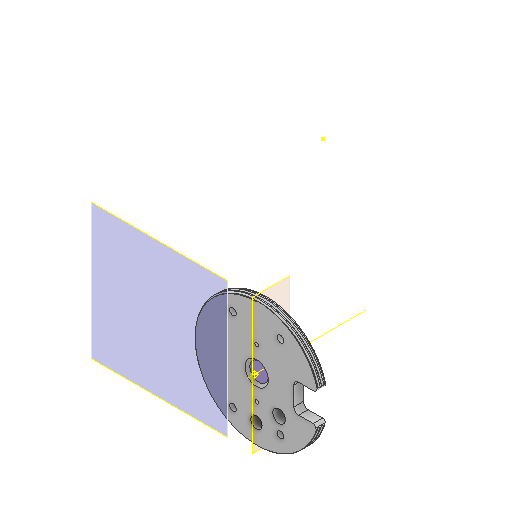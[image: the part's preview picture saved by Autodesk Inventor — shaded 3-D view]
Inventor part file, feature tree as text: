
AUTODESK INVENTOR PART (.ipt)
format: ipt  version: 2022 (Build 260153000, 153)  size: 476,672 bytes
history: native  units: in
note: dims shown in document units (in); Inventor stores cm internally (conversion verified against a paired STEP export)
features: sketch x13, reference x13, extrude x11, other x8, plane x5, projected_geometry x2, chamfer x1
ambient origin geometry x8: Origin, YZ Plane, XZ Plane, XY Plane, X Axis, Y Axis, Z Axis, Center Point
bodies: Solid1 (feature_tree)
feature tree (53):
  plane  "Work Plane1"
  extrude  "Extrusion1"  Depth=0.315in
  extrude  "Extrusion2"  Depth=1.0in
  plane  "Arbeitsebene4"
  extrude  "Extrusion5"  TaperAngle=0.0deg  [1 undecoded]
  plane  "Arbeitsebene3"
  plane  "Arbeitsebene2"
  extrude  "Extrusion7"  Depth=0.0004in TaperAngle=0.0deg
  extrude  "Extrusion10"  Depth=0.0394in TaperAngle=0.0deg
  extrude  "Extrusion13"  TaperAngle=45.0deg  [1 undecoded]
  other  "Arbeitsachse1"
  other  "Arbeitspunkt1"
  plane  "Arbeitsebene5"
  sketch  "Skizze16"  dims[d78=0.0197in d79=0.0587in]
  other  "Spirale1"
  extrude  "Extrusion14"  Depth=0.0587in
  extrude  "Extrusion16"  Depth=0.3937in TaperAngle=0.0deg
  extrude  "Extrusion17"  Depth=0.0394in TaperAngle=0.0deg
  extrude  "Extrusion18"  Depth=0.0197in
  extrude  "Extrusion19"  Depth=0.1181in TaperAngle=0.0deg
  chamfer  "Fase4"  Distance=0.1181in
  sketch  "Sketch1"  dims[d0=0.1969in d1=0.0in d2=0.315in]
  reference  "Reference1"
  reference  "Reference2"
  reference  "Reference3"
  reference  "Reference4"
  reference  "Reference5"
  reference  "Reference6"
  reference  "Reference7"
  reference  "Reference8"
  sketch  "Sketch2"  dims[d3=0.311in d4=1.0in d5=-0.0137in]
  sketch  "Sketch7"  dims[d30=0.1102in d31=0.0in d32=0.0in]
  sketch  "Sketch9"  dims[d37=0.0787in d38=0.0004in d39=0.0in]
  sketch  "Skizze12"  dims[d51=0.0394in d52=0.0in d69=0.3543in d70=0.0in]
  sketch  "Skizze15"  dims[d76=0.0276in d77=45.0deg]
  projected_geometry  "Projizierte Kontur3"
  sketch  "Skizze17"  dims[d80=0.0591in d81=0.3937in d82=0.9843in d83=0.0in d84=90.0deg d85=90.0deg d86=0.0in d87=0.0in d88=0.3937in d89=0.0in]
  sketch  "Skizze18"  dims[d92=0.0in d93=0.0in d94=0.0394in d95=0.0in]
  projected_geometry  "Projizierte Kontur4"
  sketch  "Skizze20"  dims[d96=0.0197in d97=0.0197in]
  sketch  "Skizze21"  dims[d98=0.0197in d99=0.1181in d100=0.0in d101=0.1181in d102=0.0in]
  sketch  "Skizze22"  dims[d103=0.0394in d104=0.0787in d105=45.0deg]
  reference  "Referenz30"
  reference  "Referenz31"
  reference  "Referenz32"
  sketch  "Skizze23"
  reference  "Referenz33"
  reference  "Referenz34"
  other  "Assembly1"
  other  "Assembly_MANATEE_V0_Manatee_middle2_v0_18:1"
  other  "<userpath>\Documents\GitHub\Matchboxscope\INVENTOR\Anglerfish_bonne_mamman_m12large_v0.iam"
  other  "Anglerfish_bonne_mamman_m12large_v0.iam"
  other  "00_CCTV_M12_VCM_large:1"
note: 2 required parameter values undecoded (feature->parameter linkage not recoverable at this tier; creation-order binding heuristic only, values carry confidence <= 0.55)
